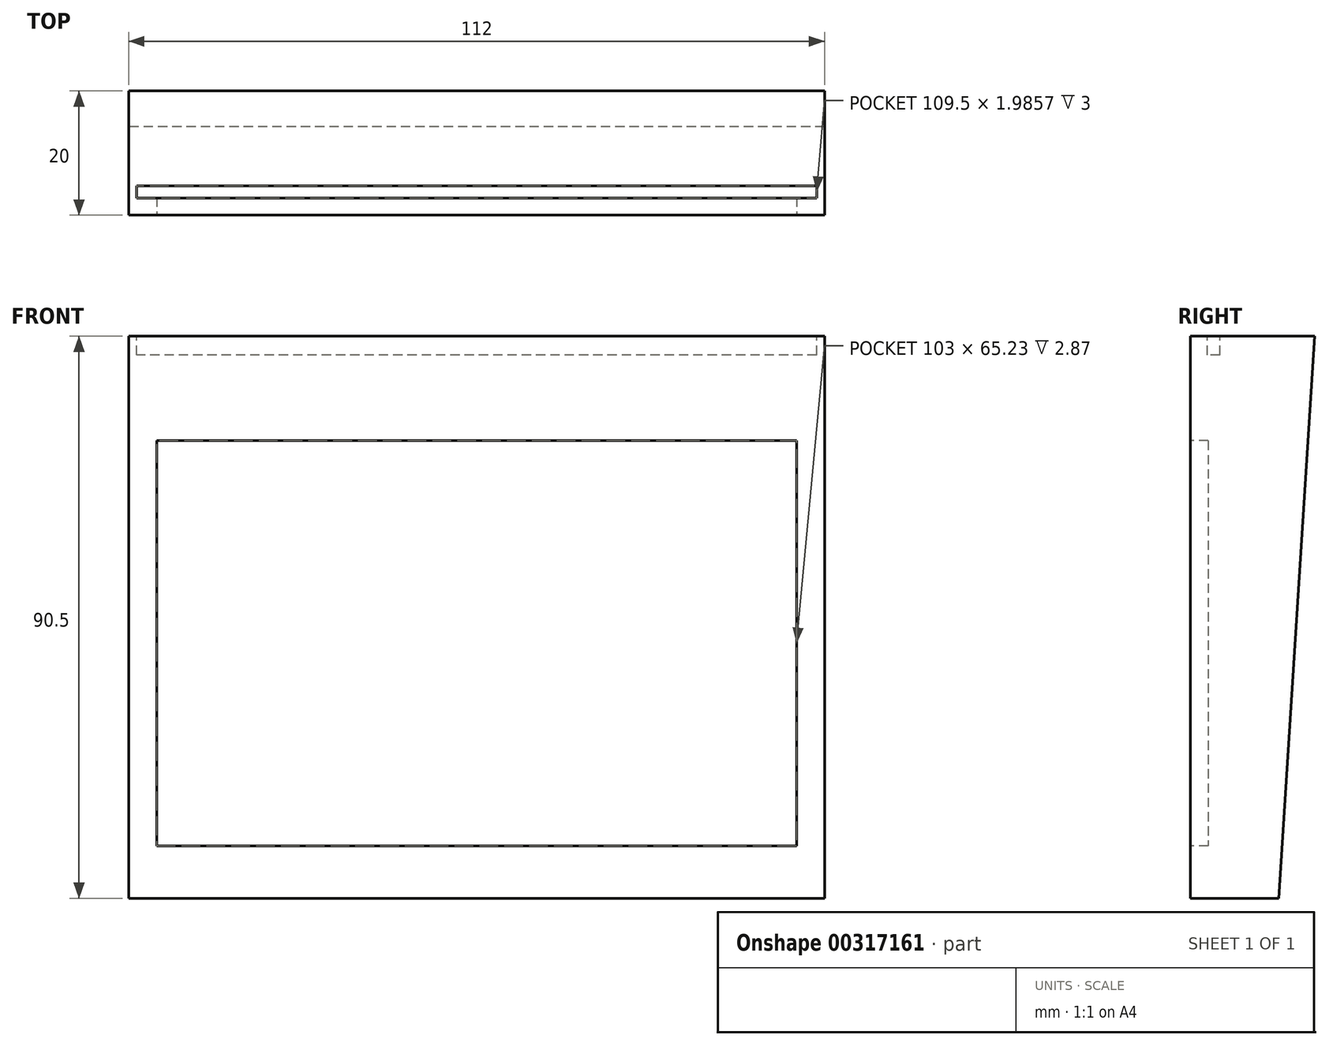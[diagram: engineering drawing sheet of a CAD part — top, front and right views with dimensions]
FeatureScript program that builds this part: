
annotation { "Feature Type Name" : "Feature", "Feature Type Description" : "" }
export const myFeature = defineFeature(function(context is Context, id is Id, definition is map)
    precondition{}
    {
        {
            var Q0;
            Q0=qCreatedBy(makeId("Front.planeOp"),FACE);
            var sketch = newSketch(context, id + "F0", { "sketchPlane" : qUnion([Q0])});
            skLineSegment(sketch, "E0.bottom", {"start": v(56, 45.25) * mm, "end": v(-56, 45.25) * mm});
            skLineSegment(sketch, "E0.top", {"start": v(56, -45.25) * mm, "end": v(-56, -45.25) * mm});
            skLineSegment(sketch, "E0.left", {"start": v(56, 45.25) * mm, "end": v(56, -45.25) * mm});
            skLineSegment(sketch, "E0.right", {"start": v(-56, 45.25) * mm, "end": v(-56, -45.25) * mm});
            skPoint(sketch, "E0.middle", {"position": v(0, 0) * mm});
            skSolve(sketch);
        }
        {
            var Q0;
            Q0 = qSketchRegion(id + "F0", true);
            extrude(context, id + "F1", {"entities" : qUnion([Q0]), "depth" : 20 * mm});
        }
        {
            var Q0;
            Q0=makeQuery(id+"F1.opExtrude","SWEPT_FACE",FACE,{"disambiguationData":[OSD([sQuery(id+"F0.wireOp",EDGE,"E0.right")])]});
            var sketch = newSketch(context, id + "F2", { "sketchPlane" : qUnion([Q0])});
            skLineSegment(sketch, "E1", {"start": v(0, 45.25) * mm, "end": v(0, -45.25) * mm});
            skLineSegment(sketch, "E2", {"start": v(0, -45.25) * mm, "end": v(5.75, -45.25) * mm});
            skLineSegment(sketch, "E3", {"start": v(5.75, -45.25) * mm, "end": v(0, 45.25) * mm});
            skSolve(sketch);
        }
        {
            var Q0;
            Q0 = qSketchRegion(id + "F2", true);
            extrude(context, id + "F3", {"entities" : qUnion([Q0]), "operationType" : NewBodyOperationType.REMOVE, "oppositeDirection" : true, "depth" : 200 * mm});
        }
        {
            var Q0;
            Q0=makeQuery(id+"F1.opExtrude","CAP_FACE",FACE,{"disambiguationData":[OSD([sQuery(id+"F0.wireOp",EDGE,"E0.bottom"),sQuery(id+"F0.wireOp",EDGE,"E0.top"),sQuery(id+"F0.wireOp",EDGE,"E0.left"),sQuery(id+"F0.wireOp",EDGE,"E0.right")])],"isStart":false});
            var sketch = newSketch(context, id + "F4", { "sketchPlane" : qUnion([Q0])});
            skLineSegment(sketch, "E4.bottom", {"start": v(-51.5, 28.43) * mm, "end": v(51.5, 28.43) * mm});
            skLineSegment(sketch, "E4.top", {"start": v(-51.5, -36.8) * mm, "end": v(51.5, -36.8) * mm});
            skLineSegment(sketch, "E4.left", {"start": v(-51.5, 28.43) * mm, "end": v(-51.5, -36.8) * mm});
            skLineSegment(sketch, "E4.right", {"start": v(51.5, 28.43) * mm, "end": v(51.5, -36.8) * mm});
            skSolve(sketch);
        }
        {
            var Q0;
            Q0 = qSketchRegion(id + "F4", true);
            extrude(context, id + "F5", {"entities" : qUnion([Q0]), "operationType" : NewBodyOperationType.REMOVE, "oppositeDirection" : true, "depth" : 2.87 * mm});
        }
        {
            var Q0;
            Q0=makeQuery(id+"F1.opExtrude","SWEPT_FACE",FACE,{"disambiguationData":[OSD([sQuery(id+"F0.wireOp",EDGE,"E0.bottom")])]});
            var sketch = newSketch(context, id + "F6", { "sketchPlane" : qUnion([Q0])});
            skLineSegment(sketch, "E5.bottom", {"start": v(54.75, -15.26) * mm, "end": v(-54.75, -15.26) * mm});
            skLineSegment(sketch, "E5.top", {"start": v(54.75, -17.25) * mm, "end": v(-54.75, -17.25) * mm});
            skLineSegment(sketch, "E5.left", {"start": v(54.75, -15.26) * mm, "end": v(54.75, -17.25) * mm});
            skLineSegment(sketch, "E5.right", {"start": v(-54.75, -15.26) * mm, "end": v(-54.75, -17.25) * mm});
            skPoint(sketch, "E5.middle", {"position": v(0, -16.26) * mm});
            skSolve(sketch);
        }
        {
            var Q0;
            Q0 = qSketchRegion(id + "F6", true);
            extrude(context, id + "F7", {"entities" : qUnion([Q0]), "operationType" : NewBodyOperationType.REMOVE, "oppositeDirection" : true, "depth" : 3 * mm});
        }
    });
